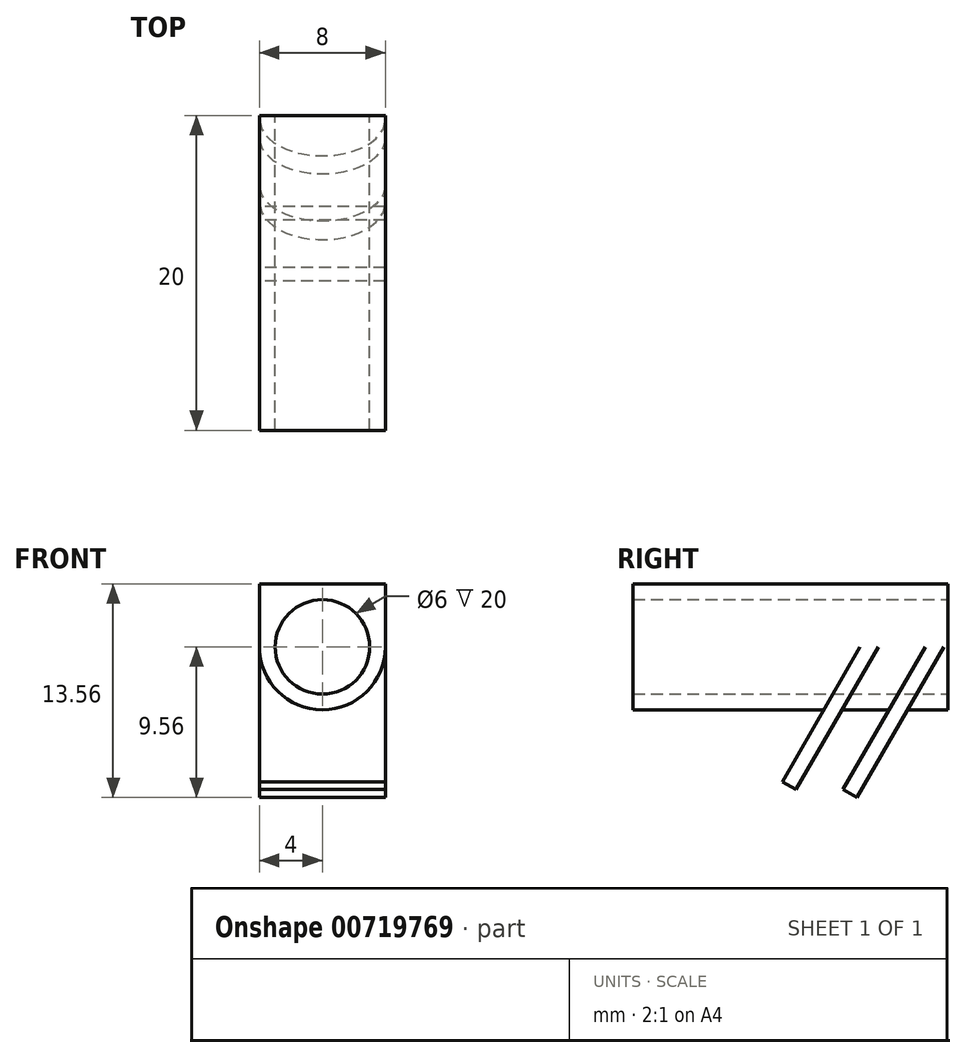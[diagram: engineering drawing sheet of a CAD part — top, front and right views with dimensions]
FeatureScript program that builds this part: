
annotation { "Feature Type Name" : "Feature", "Feature Type Description" : "" }
export const myFeature = defineFeature(function(context is Context, id is Id, definition is map)
    precondition{}
    {
        {
            var Q0;
            Q0=qCreatedBy(makeId("Front.planeOp"),FACE);
            var sketch = newSketch(context, id + "F0", { "sketchPlane" : qUnion([Q0])});
            skCircle(sketch, "E0", {"center": v(0, 0) * mm, "radius": 3 * mm});
            skCircle(sketch, "E1", {"center": v(0, 0) * mm, "radius": 4 * mm});
            skLineSegment(sketch, "E2", {"start": v(4, 0) * mm, "end": v(4, 4) * mm});
            skLineSegment(sketch, "E3", {"start": v(4, 4) * mm, "end": v(0, 4) * mm});
            skLineSegment(sketch, "E4", {"start": v(0, 4) * mm, "end": v(-4, 4) * mm});
            skLineSegment(sketch, "E5", {"start": v(-4, 4) * mm, "end": v(-4, 0) * mm});
            skSolve(sketch);
        }
        {
            var Q0;
            Q0=makeQuery(id+"F0.imprint","IMPRINT",FACE,{"disambiguationData":[TD([[makeQuery(id+"F0.imprint","IMPRINT",EDGE,{"derivedFrom":sQuery(id+"F0.wireOp",EDGE,"E0")}),-1.0]])]});
            extrude(context, id + "F1", {"entities" : qUnion([Q0]), "depth" : 20 * mm, "offsetDistance" : 25 * mm});
        }
        {
            var Q0;
            Q0=qCreatedBy(makeId("Right.planeOp"),FACE);
            var sketch = newSketch(context, id + "F2", { "sketchPlane" : qUnion([Q0])});
            skLineSegment(sketch, "E6", {"start": v(0, 0) * mm, "end": v(0, -3) * mm});
            skLineSegment(sketch, "E7", {"start": v(0, -3) * mm, "end": v(-3.15, -3) * mm});
            skLineSegment(sketch, "E8", {"start": v(-3.15, -3) * mm, "end": v(-6.65, -9.06) * mm});
            skLineSegment(sketch, "E9", {"start": v(-6.65, -9.06) * mm, "end": v(-5.79, -9.56) * mm});
            skLineSegment(sketch, "E10", {"start": v(-5.79, -9.56) * mm, "end": v(-2, -3) * mm});
            skLineSegment(sketch, "E11", {"start": v(-3.15, -3) * mm, "end": v(-6.15, -3) * mm});
            skLineSegment(sketch, "E12", {"start": v(-6.15, -3) * mm, "end": v(-9.65, -9.06) * mm});
            skLineSegment(sketch, "E13", {"start": v(-9.65, -9.06) * mm, "end": v(-10.52, -8.56) * mm});
            skLineSegment(sketch, "E14", {"start": v(-10.52, -8.56) * mm, "end": v(-7.3, -3) * mm});
            skLineSegment(sketch, "E15", {"start": v(-7.3, -3) * mm, "end": v(-6.15, -3) * mm});
            skSolve(sketch);
        }
        {
            var Q0;
            {var subQ0=sQuery(id+"F2.wireOp",EDGE,"E8");Q0=makeQuery(id+"F2.imprint","IMPRINT",FACE,{"disambiguationData":[TD([[makeQuery(id+"F2.imprint","IMPRINT",EDGE,{"derivedFrom":subQ0}),1.0]])]});}
            var Q1;
            Q1=makeQuery(id+"F2.imprint","IMPRINT",FACE,{"disambiguationData":[TD([[makeQuery(id+"F2.imprint","IMPRINT",EDGE,{"derivedFrom":sQuery(id+"F2.wireOp",EDGE,"E12")}),-1.0]])]});
            extrude(context, id + "F3", {"entities" : qUnion([Q0, Q1]), "operationType" : NewBodyOperationType.ADD, "depth" : 4 * mm, "offsetDistance" : 25 * mm, "hasSecondDirection" : true, "secondDirectionOppositeDirection" : true, "secondDirectionDepth" : 4 * mm});
        }
        {
            var Q0;
            Q0=makeQuery(id+"F3.opExtrude","SWEPT_FACE",FACE,{"disambiguationData":[OSD([sQuery(id+"F2.wireOp",EDGE,"E10")])]});
            cPlane(context, id + "F4", {"entities" : qUnion([Q0]), "cplaneType" : CPlaneType.OFFSET, "offset" : 0 * mm, "width" : 150 * mm, "height" : 150 * mm});
        }
        {
            var Q0;
            Q0=qCreatedBy(id+"F4.planeOp",FACE);
            var sketch = newSketch(context, id + "F5", { "sketchPlane" : qUnion([Q0])});
            skLineSegment(sketch, "E16", {"start": v(4, 0) * mm, "end": v(4, -5) * mm});
            skLineSegment(sketch, "E17", {"start": v(4, -5) * mm, "end": v(2, -5) * mm});
            skLineSegment(sketch, "E18", {"start": v(2, -5) * mm, "end": v(4, 0) * mm});
            skLineSegment(sketch, "E19.MirrorCS", {"start": v(-4, 0) * mm, "end": v(-4, -5) * mm});
            skLineSegment(sketch, "E20.MirrorCS", {"start": v(-4, -5) * mm, "end": v(-2, -5) * mm});
            skLineSegment(sketch, "E21.MirrorCS", {"start": v(-2, -5) * mm, "end": v(-4, 0) * mm});
            skSolve(sketch);
        }
        {
            var Q0;
            Q0=qSketchRegion(id+"F5",true);
            extrude(context, id + "F6", {"entities" : qUnion([Q0]), "operationType" : NewBodyOperationType.ADD, "oppositeDirection" : true, "depth" : 1 * mm, "offsetDistance" : 25 * mm});
        }
        {
            var Q0;
            Q0=makeQuery(id+"F3.opExtrude","SWEPT_FACE",FACE,{"disambiguationData":[OSD([sQuery(id+"F2.wireOp",EDGE,"E12")])]});
            cPlane(context, id + "F7", {"entities" : qUnion([Q0]), "cplaneType" : CPlaneType.OFFSET, "offset" : 0 * mm, "width" : 150 * mm, "height" : 150 * mm});
        }
        {
            var Q0;
            Q0=qCreatedBy(id+"F7.planeOp",FACE);
            var sketch = newSketch(context, id + "F8", { "sketchPlane" : qUnion([Q0])});
            skLineSegment(sketch, "E22", {"start": v(4, -2) * mm, "end": v(4, -7) * mm});
            skLineSegment(sketch, "E23", {"start": v(4, -7) * mm, "end": v(2, -7) * mm});
            skLineSegment(sketch, "E24", {"start": v(2, -7) * mm, "end": v(4, -2) * mm});
            skLineSegment(sketch, "E25.MirrorCS", {"start": v(-2, -7) * mm, "end": v(-4, -2) * mm});
            skLineSegment(sketch, "E26.MirrorCS", {"start": v(-4, -2) * mm, "end": v(-4, -7) * mm});
            skLineSegment(sketch, "E27.MirrorCS", {"start": v(-4, -7) * mm, "end": v(-2, -7) * mm});
            skSolve(sketch);
        }
        {
            var Q0;
            Q0=qSketchRegion(id+"F8",true);
            extrude(context, id + "F9", {"entities" : qUnion([Q0]), "operationType" : NewBodyOperationType.ADD, "oppositeDirection" : true, "depth" : 1 * mm, "offsetDistance" : 25 * mm});
        }
        {
            var Q0;
            Q0=qSketchRegion(id+"F0",true);
            extrude(context, id + "F10", {"entities" : qUnion([Q0]), "operationType" : NewBodyOperationType.ADD, "depth" : 20 * mm, "offsetDistance" : 25 * mm});
        }
    });
